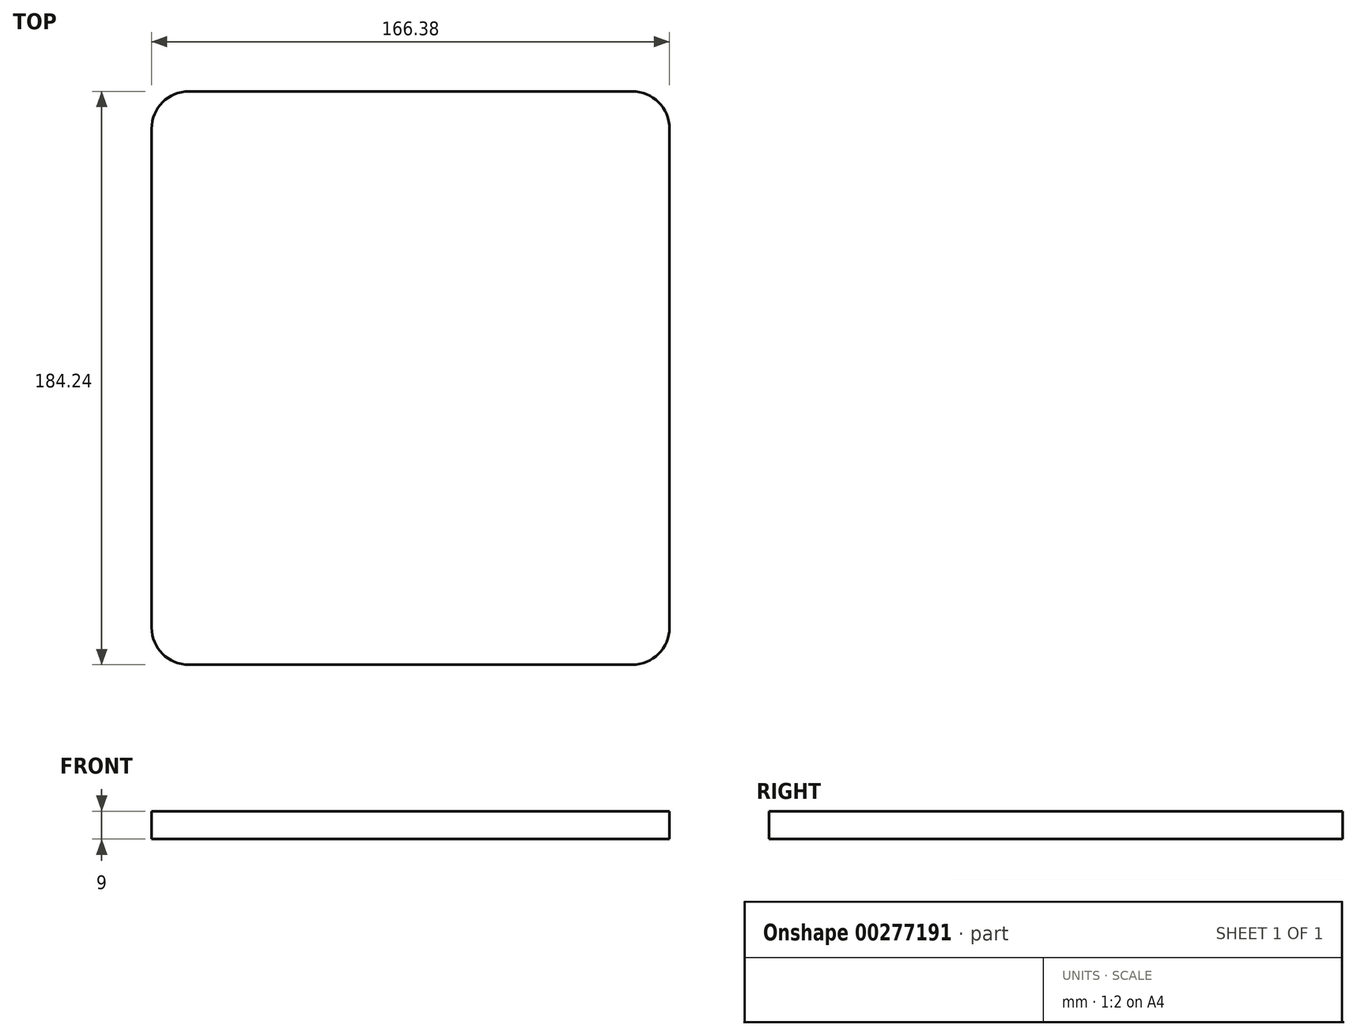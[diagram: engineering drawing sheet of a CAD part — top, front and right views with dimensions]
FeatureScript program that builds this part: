
annotation { "Feature Type Name" : "Feature", "Feature Type Description" : "" }
export const myFeature = defineFeature(function(context is Context, id is Id, definition is map)
    precondition{}
    {
        {
            var Q0;
            Q0=qCreatedBy(makeId("Top.planeOp"),FACE);
            var sketch = newSketch(context, id + "F0", { "sketchPlane" : qUnion([Q0])});
            skLineSegment(sketch, "E0.bottom", {"start": v(83.19, 92.12) * mm, "end": v(-83.19, 92.12) * mm});
            skLineSegment(sketch, "E0.top", {"start": v(83.19, -92.12) * mm, "end": v(-83.19, -92.12) * mm});
            skLineSegment(sketch, "E0.left", {"start": v(83.19, 92.12) * mm, "end": v(83.19, -92.12) * mm});
            skLineSegment(sketch, "E0.right", {"start": v(-83.19, 92.12) * mm, "end": v(-83.19, -92.12) * mm});
            skPoint(sketch, "E0.middle", {"position": v(0, 0) * mm});
            skSolve(sketch);
        }
        {
            var Q0;
            Q0 = qSketchRegion(id + "F0", true);
            extrude(context, id + "F1", {"entities" : qUnion([Q0]), "depth" : 9 * mm});
        }
        {
            var Q0;
            Q0=makeQuery(id+"F1.opExtrude","SWEPT_EDGE",EDGE,{"disambiguationData":[OSD([sQuery(id+"F0.wireOp",EDGE,"E0.bottom"),sQuery(id+"F0.wireOp",EDGE,"E0.right")])]});
            var Q1;
            Q1=makeQuery(id+"F1.opExtrude","SWEPT_EDGE",EDGE,{"disambiguationData":[OSD([sQuery(id+"F0.wireOp",EDGE,"E0.top"),sQuery(id+"F0.wireOp",EDGE,"E0.right")])]});
            var Q2;
            Q2=makeQuery(id+"F1.opExtrude","SWEPT_EDGE",EDGE,{"disambiguationData":[OSD([sQuery(id+"F0.wireOp",EDGE,"E0.top"),sQuery(id+"F0.wireOp",EDGE,"E0.left")])]});
            var Q3;
            Q3=makeQuery(id+"F1.opExtrude","SWEPT_EDGE",EDGE,{"disambiguationData":[OSD([sQuery(id+"F0.wireOp",EDGE,"E0.bottom"),sQuery(id+"F0.wireOp",EDGE,"E0.left")])]});
            fillet(context, id + "F2", {"entities" : qUnion([Q0, Q1, Q2, Q3]), "radius" : 12 * mm, "tangentPropagation" : true, "allowEdgeOverflow" : false});
        }
    });
